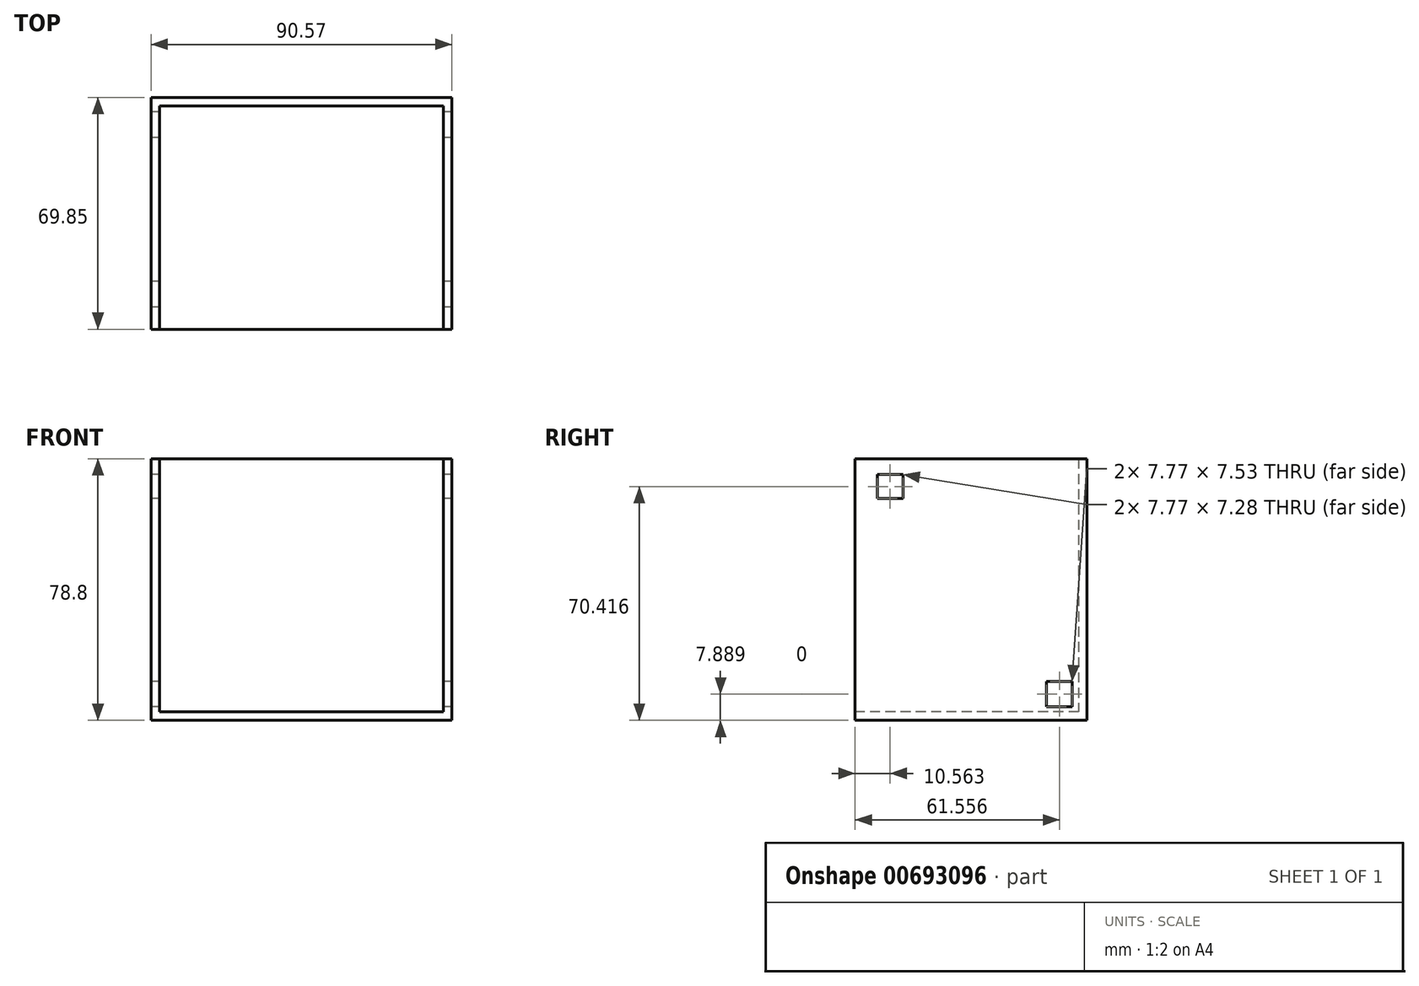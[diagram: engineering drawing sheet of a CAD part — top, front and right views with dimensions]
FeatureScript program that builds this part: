
annotation { "Feature Type Name" : "Feature", "Feature Type Description" : "" }
export const myFeature = defineFeature(function(context is Context, id is Id, definition is map)
    precondition{}
    {
        {
            var Q0;
            Q0=qCreatedBy(makeId("Front.planeOp"),FACE);
            var sketch = newSketch(context, id + "F0", { "sketchPlane" : qUnion([Q0])});
            skLineSegment(sketch, "E0.bottom", {"start": v(-43.34, 39.1) * mm, "end": v(47.23, 39.1) * mm});
            skLineSegment(sketch, "E0.top", {"start": v(-43.34, -53.42) * mm, "end": v(47.23, -53.42) * mm});
            skLineSegment(sketch, "E0.left", {"start": v(-43.34, 39.1) * mm, "end": v(-43.34, -53.42) * mm});
            skLineSegment(sketch, "E0.right", {"start": v(47.23, 39.1) * mm, "end": v(47.23, -53.42) * mm});
            skSolve(sketch);
        }
        {
            var Q0;
            Q0 = qSketchRegion(id + "F0", true);
            extrude(context, id + "F1", {"entities" : qUnion([Q0]), "oppositeDirection" : true, "depth" : 69.85 * mm, "offsetDistance" : 25.4 * mm});
        }
        {
            var Q0;
            Q0=makeQuery(id+"F1.opExtrude","CAP_FACE",FACE,{"disambiguationData":[OSD([sQuery(id+"F0.wireOp",EDGE,"E0.bottom"),sQuery(id+"F0.wireOp",EDGE,"E0.top"),sQuery(id+"F0.wireOp",EDGE,"E0.left"),sQuery(id+"F0.wireOp",EDGE,"E0.right")])],"isStart":true});
            shell(context, id + "F2", {"entities" : qUnion([Q0]), "thickness" : 2.54 * mm});
        }
        {
            var Q0;
            Q0=makeQuery(id+"F1.opExtrude","SWEPT_FACE",FACE,{"disambiguationData":[OSD([sQuery(id+"F0.wireOp",EDGE,"E0.bottom")])]});
            var sketch = newSketch(context, id + "F3", { "sketchPlane" : qUnion([Q0])});
            skSolve(sketch);
        }
        {
            var Q0;
            {var subQ0=sQuery(id+"F0.wireOp",EDGE,"E0.bottom");Q0=makeQuery(id+"F3.imprint","IMPRINT",FACE,{"disambiguationData":[TD([[makeQuery(id+"F3.imprint","IMPRINT",EDGE,{"derivedFrom":makeQuery(id+"F1.opExtrude","CAP_EDGE",EDGE,{"disambiguationData":[OSD([subQ0])],"isStart":true})}),1.0]])]});}
            extrude(context, id + "F4", {"entities" : qUnion([Q0]), "operationType" : NewBodyOperationType.REMOVE, "oppositeDirection" : true, "depth" : 13.72 * mm, "offsetDistance" : 25.4 * mm});
        }
        {
            var Q0;
            Q0=makeQuery(id+"F1.opExtrude","SWEPT_FACE",FACE,{"disambiguationData":[OSD([sQuery(id+"F0.wireOp",EDGE,"E0.left")])]});
            var sketch = newSketch(context, id + "F5", { "sketchPlane" : qUnion([Q0])});
            skLineSegment(sketch, "E1.bottom", {"start": v(-14.45, 20.64) * mm, "end": v(-6.68, 20.64) * mm});
            skLineSegment(sketch, "E1.top", {"start": v(-14.45, 13.35) * mm, "end": v(-6.68, 13.35) * mm});
            skLineSegment(sketch, "E1.left", {"start": v(-14.45, 20.64) * mm, "end": v(-14.45, 13.35) * mm});
            skLineSegment(sketch, "E1.right", {"start": v(-6.68, 20.64) * mm, "end": v(-6.68, 13.35) * mm});
            skLineSegment(sketch, "E2.bottom", {"start": v(-65.44, -41.77) * mm, "end": v(-57.67, -41.77) * mm});
            skLineSegment(sketch, "E2.top", {"start": v(-65.44, -49.3) * mm, "end": v(-57.67, -49.3) * mm});
            skLineSegment(sketch, "E2.left", {"start": v(-65.44, -41.77) * mm, "end": v(-65.44, -49.3) * mm});
            skLineSegment(sketch, "E2.right", {"start": v(-57.67, -41.77) * mm, "end": v(-57.67, -49.3) * mm});
            skSolve(sketch);
        }
        {
            var Q0;
            Q0 = qSketchRegion(id + "F5", true);
            extrude(context, id + "F6", {"entities" : qUnion([Q0]), "operationType" : NewBodyOperationType.REMOVE, "endBound" : BoundingType.THROUGH_ALL, "oppositeDirection" : true, "depth" : 25.4 * mm, "offsetDistance" : 25.4 * mm});
        }
    });
